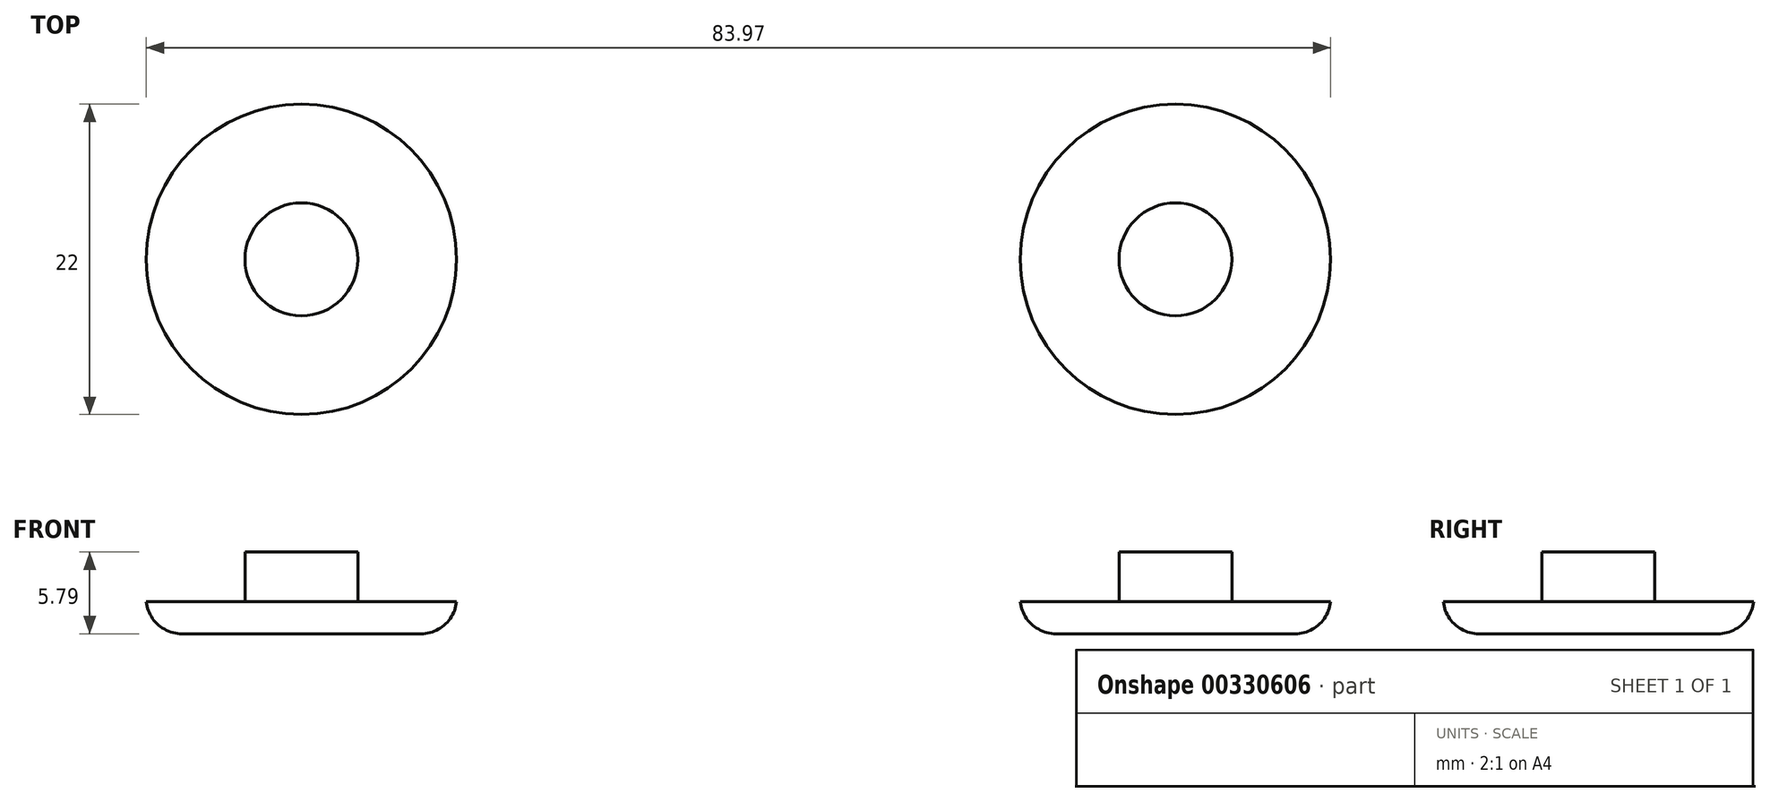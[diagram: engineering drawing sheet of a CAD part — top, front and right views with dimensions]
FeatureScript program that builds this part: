
annotation { "Feature Type Name" : "Feature", "Feature Type Description" : "" }
export const myFeature = defineFeature(function(context is Context, id is Id, definition is map)
    precondition{}
    {
        {
            var Q0;
            Q0=qCreatedBy(makeId("Top.planeOp"),FACE);
            var sketch = newSketch(context, id + "F0", { "sketchPlane" : qUnion([Q0])});
            skCircle(sketch, "E0", {"center": v(0, 0) * mm, "radius": 11 * mm});
            skSolve(sketch);
        }
        {
            var Q0;
            Q0 = qSketchRegion(id + "F0", true);
            extrude(context, id + "F1", {"entities" : qUnion([Q0]), "depth" : 2.3 * mm});
        }
        {
            var Q0;
            Q0=makeQuery(id+"F1.opExtrude","CAP_FACE",FACE,{"disambiguationData":[OSD([sQuery(id+"F0.wireOp",EDGE,"E0")])],"isStart":false});
            var sketch = newSketch(context, id + "F2", { "sketchPlane" : qUnion([Q0])});
            skCircle(sketch, "E1", {"center": v(0, 0) * mm, "radius": 4 * mm});
            skSolve(sketch);
        }
        {
            var Q0;
            Q0 = qSketchRegion(id + "F2", true);
            extrude(context, id + "F3", {"entities" : qUnion([Q0]), "operationType" : NewBodyOperationType.ADD, "depth" : 3.5 * mm});
        }
        {
            var Q0;
            Q0=makeQuery(id+"F1.opExtrude","CAP_EDGE",EDGE,{"disambiguationData":[OSD([sQuery(id+"F0.wireOp",EDGE,"E0")])],"isStart":true});
            fillet(context, id + "F4", {"entities" : qUnion([Q0]), "radius" : 2.54 * mm, "tangentPropagation" : true, "allowEdgeOverflow" : false});
        }
        {
            var Q0;
            Q0=qCreatedBy(makeId("Top.planeOp"),FACE);
            var sketch = newSketch(context, id + "F5", { "sketchPlane" : qUnion([Q0])});
            skCircle(sketch, "E2", {"center": v(61.97, 0) * mm, "radius": 11 * mm});
            skSolve(sketch);
        }
        {
            var Q0;
            Q0=makeQuery(id+"F5.imprint","IMPRINT",FACE,{"disambiguationData":[TD([[makeQuery(id+"F5.imprint","IMPRINT",EDGE,{"derivedFrom":sQuery(id+"F5.wireOp",EDGE,"E2")}),1.0]])]});
            extrude(context, id + "F6", {"entities" : qUnion([Q0]), "depth" : 2.3 * mm});
        }
        {
            var Q0;
            Q0=makeQuery(id+"F6.opExtrude","CAP_FACE",FACE,{"disambiguationData":[OSD([sQuery(id+"F5.wireOp",EDGE,"E2")])],"isStart":false});
            var sketch = newSketch(context, id + "F7", { "sketchPlane" : qUnion([Q0])});
            skCircle(sketch, "E3", {"center": v(61.97, 0) * mm, "radius": 4 * mm});
            skSolve(sketch);
        }
        {
            var Q0;
            Q0=makeQuery(id+"F7.imprint","IMPRINT",FACE,{"disambiguationData":[TD([[makeQuery(id+"F7.imprint","IMPRINT",EDGE,{"derivedFrom":sQuery(id+"F7.wireOp",EDGE,"E3")}),1.0]])]});
            extrude(context, id + "F8", {"entities" : qUnion([Q0]), "operationType" : NewBodyOperationType.ADD, "depth" : 3.5 * mm});
        }
        {
            var Q0;
            Q0=makeQuery(id+"F6.opExtrude","CAP_EDGE",EDGE,{"disambiguationData":[OSD([sQuery(id+"F5.wireOp",EDGE,"E2")])],"isStart":true});
            fillet(context, id + "F9", {"entities" : qUnion([Q0]), "radius" : 2.54 * mm, "tangentPropagation" : true, "allowEdgeOverflow" : false});
        }
    });
